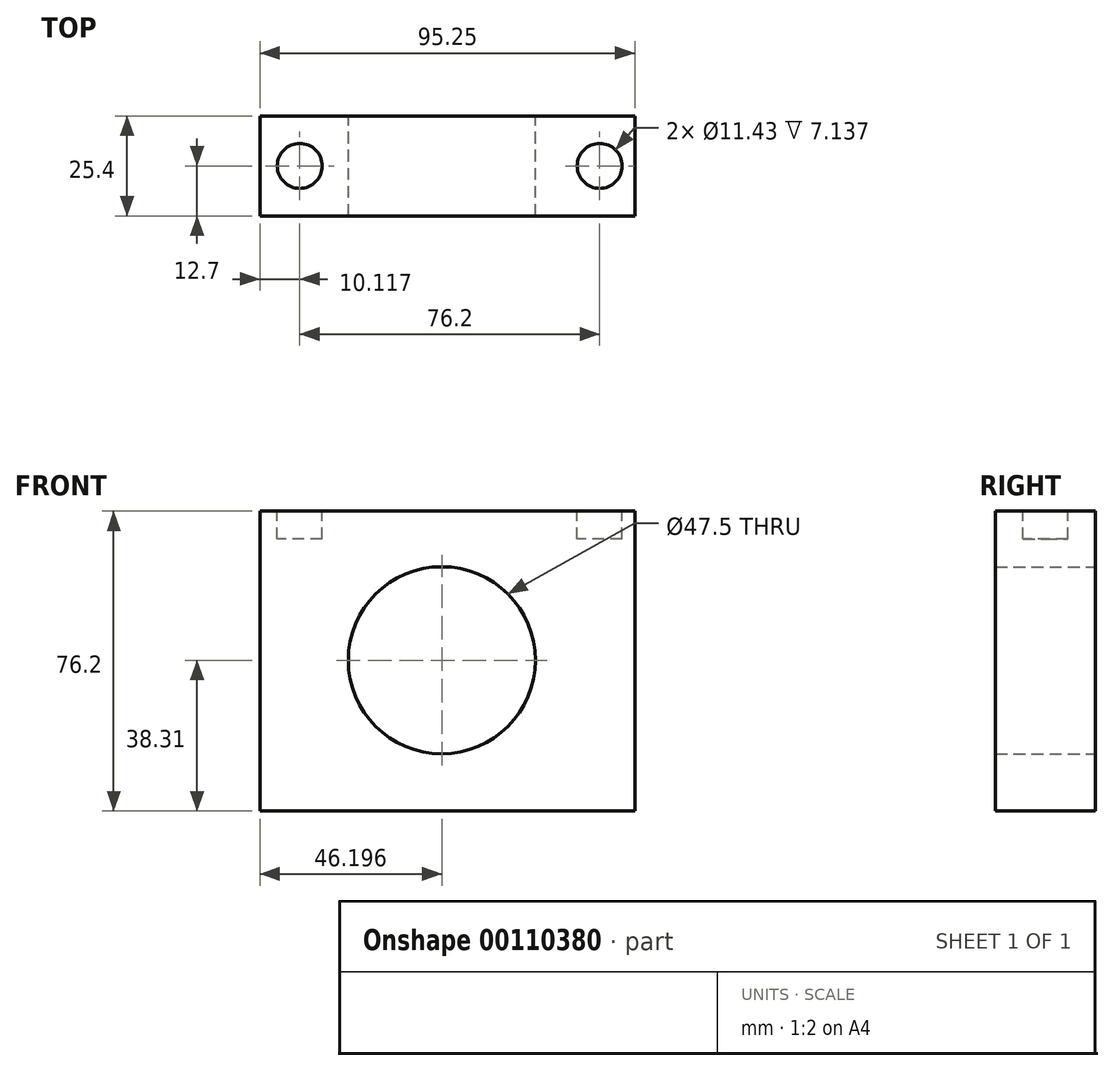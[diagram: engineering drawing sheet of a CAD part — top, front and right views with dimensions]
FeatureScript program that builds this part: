
annotation { "Feature Type Name" : "Feature", "Feature Type Description" : "" }
export const myFeature = defineFeature(function(context is Context, id is Id, definition is map)
    precondition{}
    {
        {
            var Q0;
            Q0=qCreatedBy(makeId("Front.planeOp"),FACE);
            var sketch = newSketch(context, id + "F0", { "sketchPlane" : qUnion([Q0])});
            skLineSegment(sketch, "E0", {"start": v(-27.76, 37.9) * mm, "end": v(-27.76, -38.3) * mm});
            skLineSegment(sketch, "E1", {"start": v(-27.76, 37.9) * mm, "end": v(67.5, 37.9) * mm});
            skLineSegment(sketch, "E2", {"start": v(67.5, 37.9) * mm, "end": v(67.5, -38.3) * mm});
            skLineSegment(sketch, "E3", {"start": v(67.5, -38.3) * mm, "end": v(-27.76, -38.3) * mm});
            skCircle(sketch, "E4", {"center": v(18.44, 0) * mm, "radius": 23.75 * mm});
            skSolve(sketch);
        }
        {
            var Q0;
            Q0=makeQuery(id+"F0.imprint","IMPRINT",FACE,{"disambiguationData":[TD([[makeQuery(id+"F0.imprint","IMPRINT",EDGE,{"derivedFrom":sQuery(id+"F0.wireOp",EDGE,"E0")}),1.0]])]});
            extrude(context, id + "F1", {"entities" : qUnion([Q0]), "depth" : 25.4 * mm});
        }
        {
            var Q0;
            Q0=makeQuery(id+"F1.opExtrude","SWEPT_FACE",FACE,{"disambiguationData":[OSD([sQuery(id+"F0.wireOp",EDGE,"E1")])]});
            var sketch = newSketch(context, id + "F2", { "sketchPlane" : qUnion([Q0])});
            skCircle(sketch, "E5", {"center": v(-18.52, -12.5) * mm, "radius": 3.57 * mm});
            skCircle(sketch, "E6", {"center": v(57.68, -11.95) * mm, "radius": 3.57 * mm});
            skSolve(sketch);
        }
        {
            var Q0;
            Q0=makeQuery(id+"F2.imprint","IMPRINT",FACE,{"disambiguationData":[TD([[makeQuery(id+"F2.imprint","IMPRINT",EDGE,{"derivedFrom":sQuery(id+"F2.wireOp",EDGE,"E6")}),1.0]])]});
            var Q1;
            Q1 = qConstructionFilter(qBodyType(qCreatedBy(id + "F2" ,EDGE), BodyType.WIRE), ConstructionObject.NO);
            extrude(context, id + "F3", {"entities" : qUnion([Q0]), "operationType" : NewBodyOperationType.REMOVE, "surfaceEntities" : qUnion([Q1]), "depth" : 7.14 * mm});
        }
        {
            var Q0;
            Q0=makeQuery(id+"F1.opExtrude","SWEPT_FACE",FACE,{"disambiguationData":[OSD([sQuery(id+"F0.wireOp",EDGE,"E1")])]});
            var sketch = newSketch(context, id + "F4", { "sketchPlane" : qUnion([Q0])});
            skCircle(sketch, "E7", {"center": v(-17.64, -12.7) * mm, "radius": 5.71 * mm});
            skCircle(sketch, "E8", {"center": v(58.56, -12.7) * mm, "radius": 5.72 * mm});
            skSolve(sketch);
        }
        {
            var Q0;
            Q0 = qSketchRegion(id + "F4", true);
            extrude(context, id + "F5", {"entities" : qUnion([Q0]), "operationType" : NewBodyOperationType.REMOVE, "oppositeDirection" : true, "depth" : 7.14 * mm});
        }
    });
